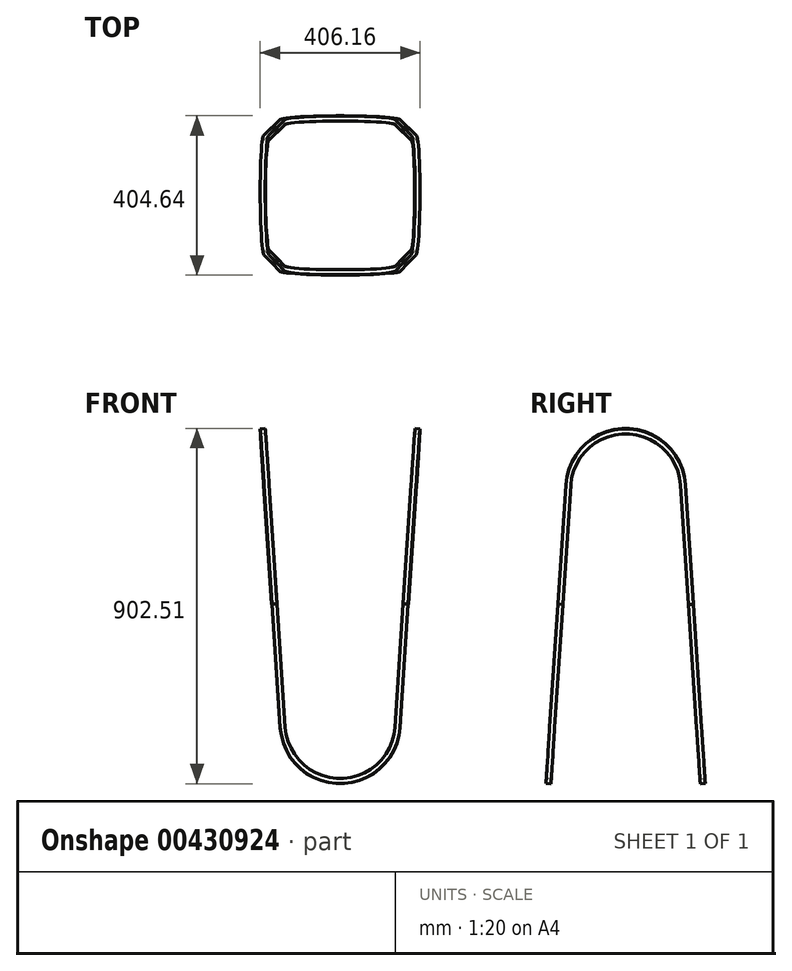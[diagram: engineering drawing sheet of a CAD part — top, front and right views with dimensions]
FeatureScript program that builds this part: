
annotation { "Feature Type Name" : "Feature", "Feature Type Description" : "" }
export const myFeature = defineFeature(function(context is Context, id is Id, definition is map)
    precondition{}
    {
        {
            var Q0;
            Q0=qCreatedBy(makeId("Front.planeOp"),FACE);
            var sketch = newSketch(context, id + "F0", { "sketchPlane" : qUnion([Q0])});
            skLineSegment(sketch, "E0", {"start": v(0, 0) * mm, "end": v(-62.1, 0) * mm});
            skSolve(sketch);
        }
        {
            var Q0;
            Q0=sQuery(id+"F0.wireOp",EDGE,"E0");
            cPlane(context, id + "F1", {"entities" : qUnion([Q0]), "cplaneType" : CPlaneType.LINE_ANGLE, "offset" : 25.4 * mm, "angle" : 183.79 * degree, "width" : 152.4 * mm, "height" : 152.4 * mm});
        }
        {
            var Q0;
            Q0=qCreatedBy(id+"F1.planeOp",FACE);
            var sketch = newSketch(context, id + "F2", { "sketchPlane" : qUnion([Q0])});
            skArc(sketch, "E1", {"start": v(-152.07, -10.07) * mm, "mid": v(0, -152.4) * mm, "end": v(152.07, -10.07) * mm});
            skLineSegment(sketch, "E2", {"start": v(-172.86, 303.96) * mm, "end": v(-152.07, -10.07) * mm});
            skLineSegment(sketch, "E3.MirrorCS", {"start": v(172.86, 303.96) * mm, "end": v(152.07, -10.07) * mm});
            skLineSegment(sketch, "E4.0", {"start": v(160.2, 304.8) * mm, "end": v(139.4, -9.23) * mm});
            skArc(sketch, "E4.1", {"start": v(-139.4, -9.23) * mm, "mid": v(0, -139.7) * mm, "end": v(139.4, -9.23) * mm});
            skLineSegment(sketch, "E4.2", {"start": v(-160.2, 304.8) * mm, "end": v(-139.4, -9.23) * mm});
            skLineSegment(sketch, "E5", {"start": v(160.2, 304.8) * mm, "end": v(172.86, 303.96) * mm});
            skLineSegment(sketch, "E6.MirrorCS", {"start": v(-160.2, 304.8) * mm, "end": v(-172.86, 303.96) * mm});
            skSolve(sketch);
        }
        {
            var Q0;
            Q0=makeQuery(id+"F2.imprint","IMPRINT",FACE,{"disambiguationData":[TD([[makeQuery(id+"F2.imprint","IMPRINT",EDGE,{"derivedFrom":sQuery(id+"F2.wireOp",EDGE,"E1")}),1.0]])]});
            extrude(context, id + "F3", {"entities" : qUnion([Q0]), "depth" : 12.7 * mm});
        }
        {
            var Q0;
            Q0=makeQuery(id+"F3.opExtrude","SWEPT_EDGE",EDGE,{"disambiguationData":[OSD([sQuery(id+"F2.wireOp",EDGE,"E2"),sQuery(id+"F2.wireOp",EDGE,"E6.MirrorCS")])]});
            cPlane(context, id + "F4", {"entities" : qUnion([Q0]), "cplaneType" : CPlaneType.LINE_ANGLE, "offset" : 25.4 * mm, "angle" : 93.79 * degree, "oppositeDirection" : true, "width" : 152.4 * mm, "height" : 152.4 * mm});
        }
        {
            var Q0;
            Q0=qCreatedBy(id+"F4.planeOp",FACE);
            var sketch = newSketch(context, id + "F5", { "sketchPlane" : qUnion([Q0])});
            skLineSegment(sketch, "E7", {"start": v(-20.75, 314.03) * mm, "end": v(-40.85, 618.17) * mm});
            skArc(sketch, "E8", {"start": v(-40.85, 618.17) * mm, "mid": v(-192.92, 760.52) * mm, "end": v(-344.99, 618.17) * mm});
            skLineSegment(sketch, "E9.MirrorCS", {"start": v(-365.08, 314.03) * mm, "end": v(-344.99, 618.17) * mm});
            skLineSegment(sketch, "E10.0", {"start": v(-352.41, 313.2) * mm, "end": v(-332.31, 617.33) * mm});
            skArc(sketch, "E10.1", {"start": v(-53.52, 617.33) * mm, "mid": v(-192.92, 747.82) * mm, "end": v(-332.31, 617.33) * mm});
            skLineSegment(sketch, "E10.2", {"start": v(-33.42, 313.2) * mm, "end": v(-53.52, 617.33) * mm});
            skLineSegment(sketch, "E11", {"start": v(-352.41, 313.2) * mm, "end": v(-365.08, 314.03) * mm});
            skLineSegment(sketch, "E12", {"start": v(-20.75, 314.03) * mm, "end": v(-33.42, 313.2) * mm});
            skSolve(sketch);
        }
        {
            var Q0;
            Q0=makeQuery(id+"F5.imprint","IMPRINT",FACE,{"disambiguationData":[TD([[makeQuery(id+"F5.imprint","IMPRINT",EDGE,{"derivedFrom":sQuery(id+"F5.wireOp",EDGE,"E7")}),1.0]])]});
            extrude(context, id + "F6", {"entities" : qUnion([Q0]), "depth" : 12.7 * mm});
        }
        {
            var Q0;
            Q0=makeQuery(id+"F6.opExtrude","SWEPT_BODY",BODY,{"disambiguationData":[OSD([sQuery(id+"F5.wireOp",EDGE,"E7"),sQuery(id+"F5.wireOp",EDGE,"E8"),sQuery(id+"F5.wireOp",EDGE,"E9.MirrorCS"),sQuery(id+"F5.wireOp",EDGE,"E10.0"),sQuery(id+"F5.wireOp",EDGE,"E10.1"),sQuery(id+"F5.wireOp",EDGE,"E10.2"),sQuery(id+"F5.wireOp",EDGE,"E11"),sQuery(id+"F5.wireOp",EDGE,"E12")])]});
            var Q1;
            Q1=qCreatedBy(makeId("Right.planeOp"),FACE);
            mirror(context, id + "F7", {"entities" : qUnion([Q0]), "mirrorPlane" : qUnion([Q1])});
        }
        {
            var Q0;
            Q0=qCreatedBy(id+"F4.planeOp",FACE);
            var sketch = newSketch(context, id + "F8", { "sketchPlane" : qUnion([Q0])});
            skLineSegment(sketch, "E13", {"start": v(-192.92, 747.82) * mm, "end": v(-192.92, 643.96) * mm});
            skSolve(sketch);
        }
        {
            var Q0;
            Q0=sQuery(id+"F8.wireOp",EDGE,"E13");
            cPlane(context, id + "F9", {"entities" : qUnion([Q0]), "cplaneType" : CPlaneType.LINE_ANGLE, "offset" : 25.4 * mm, "angle" : 90 * degree, "width" : 152.4 * mm, "height" : 152.4 * mm});
        }
        {
            var Q0;
            Q0=makeQuery(id+"F3.opExtrude","SWEPT_BODY",BODY,{"disambiguationData":[OSD([sQuery(id+"F2.wireOp",EDGE,"E1"),sQuery(id+"F2.wireOp",EDGE,"E2"),sQuery(id+"F2.wireOp",EDGE,"E3.MirrorCS"),sQuery(id+"F2.wireOp",EDGE,"E4.0"),sQuery(id+"F2.wireOp",EDGE,"E4.1"),sQuery(id+"F2.wireOp",EDGE,"E4.2"),sQuery(id+"F2.wireOp",EDGE,"E5"),sQuery(id+"F2.wireOp",EDGE,"E6.MirrorCS")])]});
            var Q1;
            Q1=qCreatedBy(id+"F9.planeOp",FACE);
            mirror(context, id + "F10", {"entities" : qUnion([Q0]), "mirrorPlane" : qUnion([Q1])});
        }
    });
